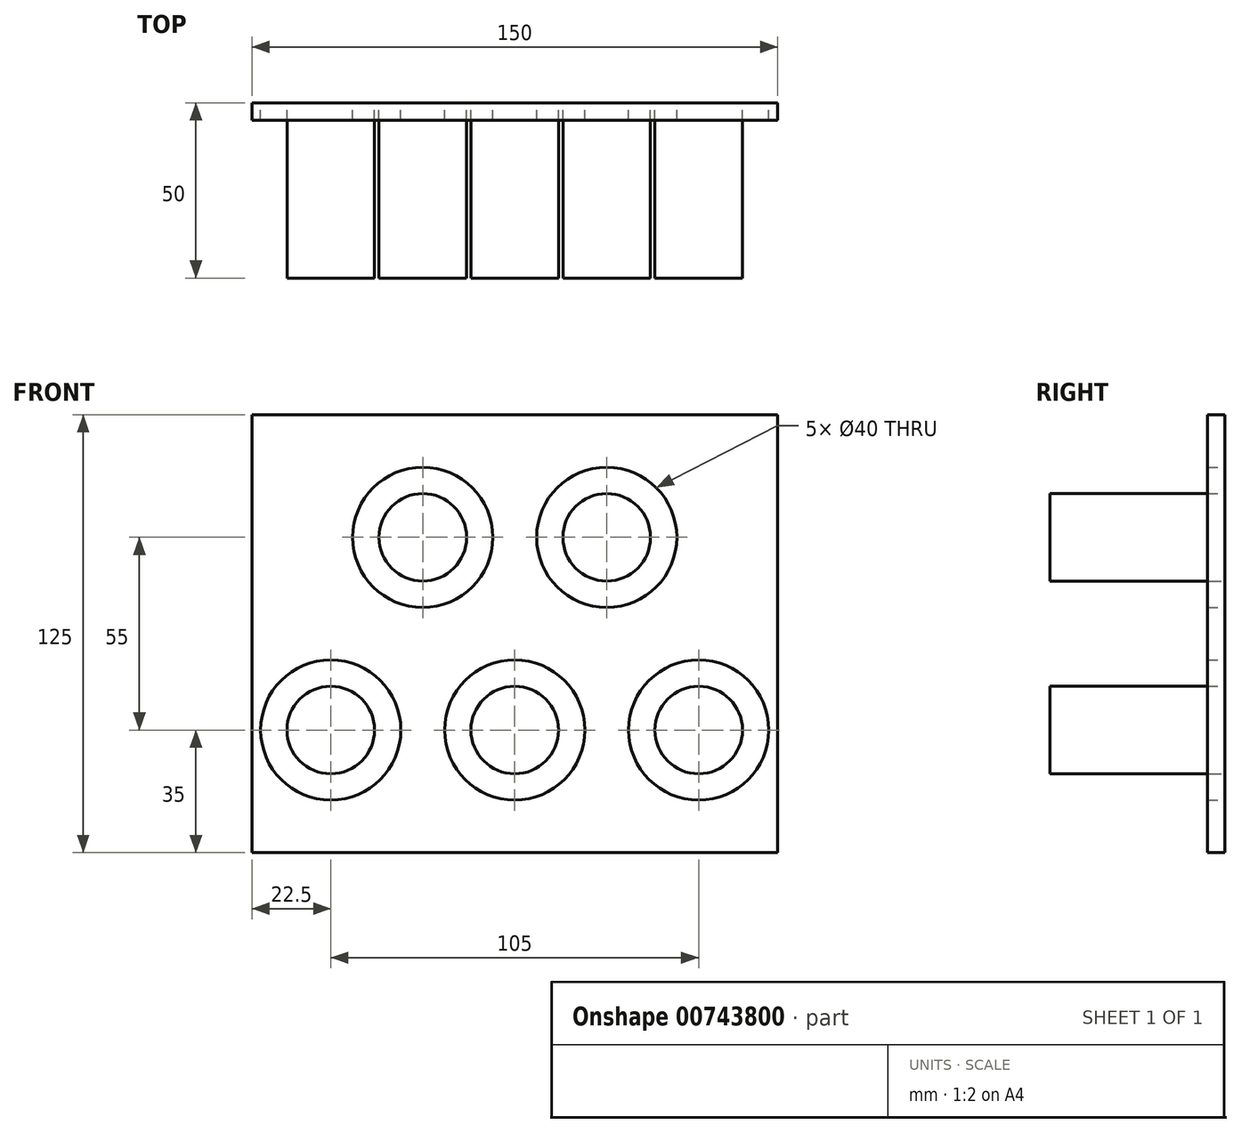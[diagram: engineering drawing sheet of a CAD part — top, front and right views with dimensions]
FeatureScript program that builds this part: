
annotation { "Feature Type Name" : "Feature", "Feature Type Description" : "" }
export const myFeature = defineFeature(function(context is Context, id is Id, definition is map)
    precondition{}
    {
        {
            var Q0;
            Q0=qCreatedBy(makeId("Front.planeOp"),FACE);
            var sketch = newSketch(context, id + "F0", { "sketchPlane" : qUnion([Q0])});
            skCircle(sketch, "E0", {"center": v(-26.25, 55) * mm, "radius": 12.5 * mm});
            skCircle(sketch, "E1", {"center": v(26.25, 55) * mm, "radius": 12.5 * mm});
            skCircle(sketch, "E2", {"center": v(0, 0) * mm, "radius": 12.5 * mm});
            skCircle(sketch, "E3", {"center": v(-52.5, 0) * mm, "radius": 12.5 * mm});
            skCircle(sketch, "E4", {"center": v(52.5, 0) * mm, "radius": 12.5 * mm});
            skLineSegment(sketch, "E5", {"start": v(-26.25, 67.5) * mm, "end": v(26.25, 67.5) * mm, "construction": true});
            skLineSegment(sketch, "E6", {"start": v(-52.5, -12.5) * mm, "end": v(52.5, -12.5) * mm, "construction": true});
            skLineSegment(sketch, "E7", {"start": v(-52.5, 0) * mm, "end": v(0, 0) * mm, "construction": true});
            skPoint(sketch, "E8", {"position": v(-26.25, 0) * mm});
            skCircle(sketch, "E9", {"center": v(-26.25, 55) * mm, "radius": 20 * mm});
            skCircle(sketch, "E10", {"center": v(26.25, 55) * mm, "radius": 20 * mm});
            skCircle(sketch, "E11", {"center": v(-52.5, 0) * mm, "radius": 20 * mm});
            skCircle(sketch, "E12", {"center": v(0, 0) * mm, "radius": 20 * mm});
            skCircle(sketch, "E13", {"center": v(52.5, 0) * mm, "radius": 20 * mm});
            skLineSegment(sketch, "E14.bottom", {"start": v(-75, 90) * mm, "end": v(75, 90) * mm});
            skLineSegment(sketch, "E14.top", {"start": v(-75, -35) * mm, "end": v(75, -35) * mm});
            skLineSegment(sketch, "E14.left", {"start": v(-75, 90) * mm, "end": v(-75, -35) * mm});
            skLineSegment(sketch, "E14.right", {"start": v(75, 90) * mm, "end": v(75, -35) * mm});
            skLineSegment(sketch, "E15", {"start": v(0, 67.5) * mm, "end": v(0, 90) * mm, "construction": true});
            skLineSegment(sketch, "E16", {"start": v(0, -12.5) * mm, "end": v(0, -35) * mm, "construction": true});
            skSolve(sketch);
        }
        {
            var Q0;
            Q0=makeQuery(id+"F0.imprint","IMPRINT",FACE,{"disambiguationData":[TD([[makeQuery(id+"F0.imprint","IMPRINT",EDGE,{"derivedFrom":sQuery(id+"F0.wireOp",EDGE,"E0")}),1.0]])]});
            var Q1;
            Q1=makeQuery(id+"F0.imprint","IMPRINT",FACE,{"disambiguationData":[TD([[makeQuery(id+"F0.imprint","IMPRINT",EDGE,{"derivedFrom":sQuery(id+"F0.wireOp",EDGE,"E1")}),1.0]])]});
            var Q2;
            Q2=makeQuery(id+"F0.imprint","IMPRINT",FACE,{"disambiguationData":[TD([[makeQuery(id+"F0.imprint","IMPRINT",EDGE,{"derivedFrom":sQuery(id+"F0.wireOp",EDGE,"E3")}),1.0]])]});
            var Q3;
            Q3=makeQuery(id+"F0.imprint","IMPRINT",FACE,{"disambiguationData":[TD([[makeQuery(id+"F0.imprint","IMPRINT",EDGE,{"derivedFrom":sQuery(id+"F0.wireOp",EDGE,"E2")}),1.0]])]});
            var Q4;
            Q4=makeQuery(id+"F0.imprint","IMPRINT",FACE,{"disambiguationData":[TD([[makeQuery(id+"F0.imprint","IMPRINT",EDGE,{"derivedFrom":sQuery(id+"F0.wireOp",EDGE,"E4")}),1.0]])]});
            extrude(context, id + "F1", {"entities" : qUnion([Q0, Q1, Q2, Q3, Q4]), "depth" : 50 * mm, "offsetDistance" : 25 * mm});
        }
        {
            var Q0;
            Q0=makeQuery(id+"F0.imprint","IMPRINT",FACE,{"disambiguationData":[TD([[makeQuery(id+"F0.imprint","IMPRINT",EDGE,{"derivedFrom":sQuery(id+"F0.wireOp",EDGE,"E9")}),-1.0]])]});
            extrude(context, id + "F2", {"entities" : qUnion([Q0]), "depth" : 5 * mm, "offsetDistance" : 25 * mm});
        }
    });
